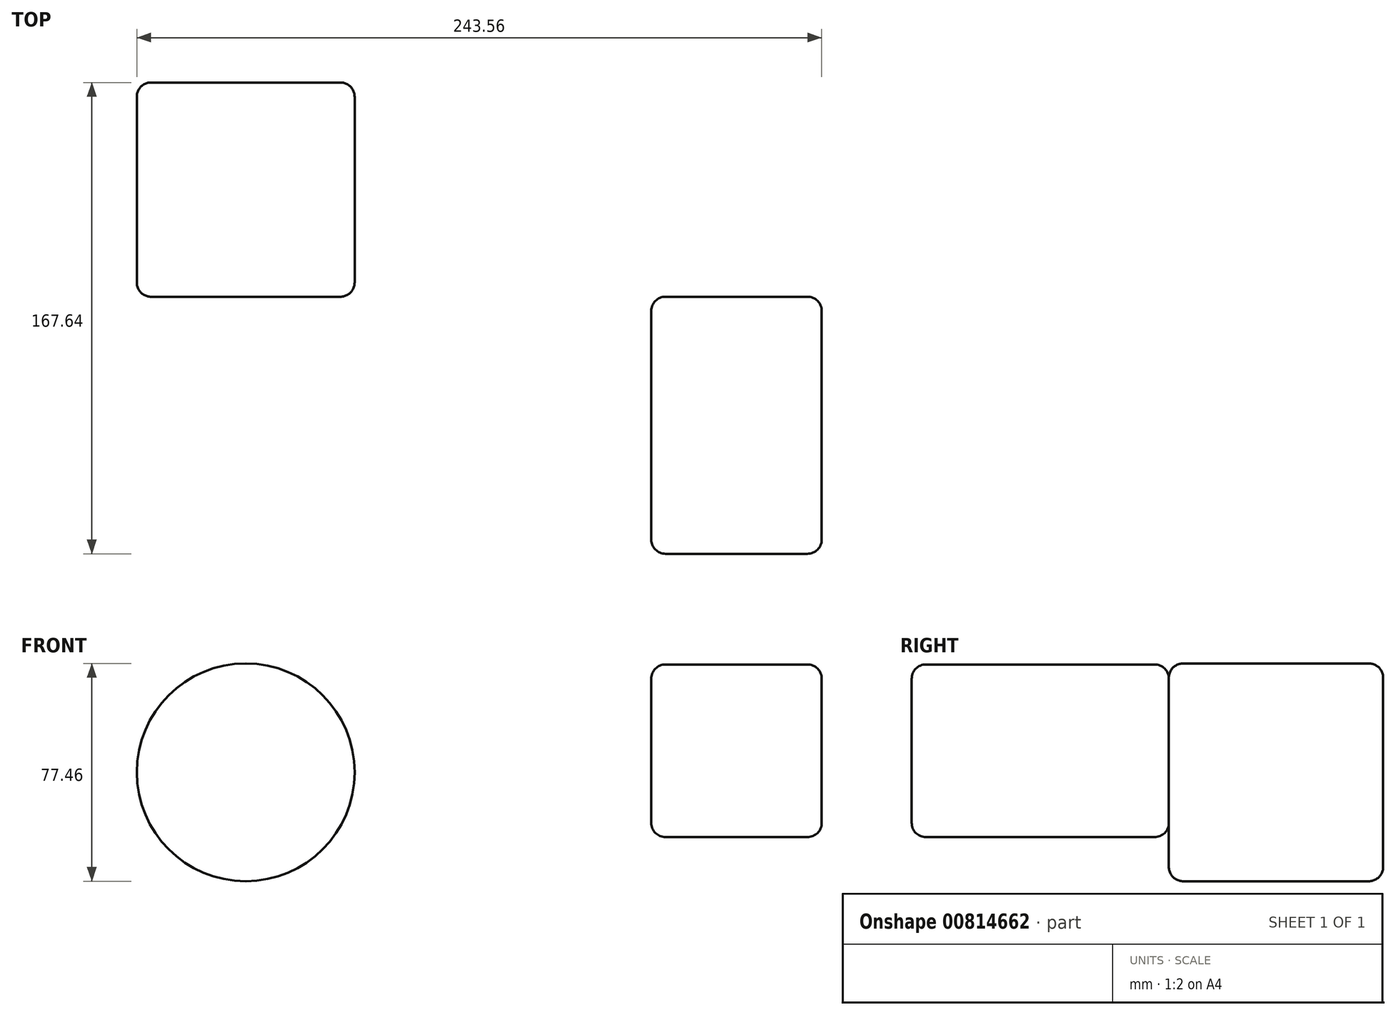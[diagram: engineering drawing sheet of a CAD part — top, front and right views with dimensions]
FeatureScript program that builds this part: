
annotation { "Feature Type Name" : "Feature", "Feature Type Description" : "" }
export const myFeature = defineFeature(function(context is Context, id is Id, definition is map)
    precondition{}
    {
        {
            var Q0;
            Q0=qCreatedBy(makeId("Front.planeOp"),FACE);
            var sketch = newSketch(context, id + "F0", { "sketchPlane" : qUnion([Q0])});
            skCircle(sketch, "E0", {"center": v(-110.61, 4.94) * mm, "radius": 38.73 * mm});
            skSolve(sketch);
        }
        {
            var Q0;
            Q0=makeQuery(id+"F0.imprint","IMPRINT",FACE,{"disambiguationData":[TD([[makeQuery(id+"F0.imprint","IMPRINT",EDGE,{"derivedFrom":sQuery(id+"F0.wireOp",EDGE,"E0")}),1.0]])]});
            extrude(context, id + "F1", {"entities" : qUnion([Q0]), "oppositeDirection" : true, "depth" : 76.2 * mm, "offsetDistance" : 25.4 * mm});
        }
        {
            var Q0;
            Q0=makeQuery(id+"F1.opExtrude","CAP_EDGE",EDGE,{"disambiguationData":[OSD([sQuery(id+"F0.wireOp",EDGE,"E0")])],"isStart":false});
            var Q1;
            Q1=makeQuery(id+"F1.opExtrude","CAP_EDGE",EDGE,{"disambiguationData":[OSD([sQuery(id+"F0.wireOp",EDGE,"E0")])],"isStart":true});
            fillet(context, id + "F2", {"entities" : qUnion([Q0, Q1]), "radius" : 5.08 * mm, "tangentPropagation" : true, "allowEdgeOverflow" : false});
        }
        {
            var Q0;
            Q0=qCreatedBy(makeId("Front.planeOp"),FACE);
            var sketch = newSketch(context, id + "F3", { "sketchPlane" : qUnion([Q0])});
            skLineSegment(sketch, "E1.bottom", {"start": v(94.22, 43.29) * mm, "end": v(33.6, 43.29) * mm});
            skLineSegment(sketch, "E1.top", {"start": v(94.22, -18.13) * mm, "end": v(33.6, -18.13) * mm});
            skLineSegment(sketch, "E1.left", {"start": v(94.22, 43.29) * mm, "end": v(94.22, -18.13) * mm});
            skLineSegment(sketch, "E1.right", {"start": v(33.6, 43.29) * mm, "end": v(33.6, -18.13) * mm});
            skSolve(sketch);
        }
        {
            var Q0;
            Q0=makeQuery(id+"F3.imprint","IMPRINT",FACE,{"disambiguationData":[TD([[makeQuery(id+"F3.imprint","IMPRINT",EDGE,{"derivedFrom":sQuery(id+"F3.wireOp",EDGE,"E1.bottom")}),1.0]])]});
            extrude(context, id + "F4", {"entities" : qUnion([Q0]), "depth" : 91.44 * mm, "offsetDistance" : 25.4 * mm});
        }
        {
            var Q0;
            Q0=makeQuery(id+"F4.opExtrude","CAP_EDGE",EDGE,{"disambiguationData":[OSD([sQuery(id+"F3.wireOp",EDGE,"E1.left")])],"isStart":false});
            var Q1;
            Q1=makeQuery(id+"F4.opExtrude","SWEPT_EDGE",EDGE,{"disambiguationData":[OSD([sQuery(id+"F3.wireOp",EDGE,"E1.top"),sQuery(id+"F3.wireOp",EDGE,"E1.left")])]});
            var Q2;
            Q2=makeQuery(id+"F4.opExtrude","CAP_EDGE",EDGE,{"disambiguationData":[OSD([sQuery(id+"F3.wireOp",EDGE,"E1.left")])],"isStart":true});
            var Q3;
            Q3=makeQuery(id+"F4.opExtrude","SWEPT_EDGE",EDGE,{"disambiguationData":[OSD([sQuery(id+"F3.wireOp",EDGE,"E1.bottom"),sQuery(id+"F3.wireOp",EDGE,"E1.left")])]});
            var Q4;
            Q4=makeQuery(id+"F4.opExtrude","CAP_EDGE",EDGE,{"disambiguationData":[OSD([sQuery(id+"F3.wireOp",EDGE,"E1.bottom")])],"isStart":true});
            var Q5;
            Q5=makeQuery(id+"F4.opExtrude","CAP_EDGE",EDGE,{"disambiguationData":[OSD([sQuery(id+"F3.wireOp",EDGE,"E1.right")])],"isStart":true});
            var Q6;
            Q6=makeQuery(id+"F4.opExtrude","CAP_EDGE",EDGE,{"disambiguationData":[OSD([sQuery(id+"F3.wireOp",EDGE,"E1.top")])],"isStart":true});
            var Q7;
            Q7=makeQuery(id+"F4.opExtrude","CAP_EDGE",EDGE,{"disambiguationData":[OSD([sQuery(id+"F3.wireOp",EDGE,"E1.right")])],"isStart":false});
            var Q8;
            Q8=makeQuery(id+"F4.opExtrude","SWEPT_EDGE",EDGE,{"disambiguationData":[OSD([sQuery(id+"F3.wireOp",EDGE,"E1.bottom"),sQuery(id+"F3.wireOp",EDGE,"E1.right")])]});
            var Q9;
            Q9=makeQuery(id+"F4.opExtrude","SWEPT_EDGE",EDGE,{"disambiguationData":[OSD([sQuery(id+"F3.wireOp",EDGE,"E1.top"),sQuery(id+"F3.wireOp",EDGE,"E1.right")])]});
            var Q10;
            Q10=makeQuery(id+"F4.opExtrude","CAP_EDGE",EDGE,{"disambiguationData":[OSD([sQuery(id+"F3.wireOp",EDGE,"E1.top")])],"isStart":false});
            var Q11;
            Q11=makeQuery(id+"F4.opExtrude","CAP_EDGE",EDGE,{"disambiguationData":[OSD([sQuery(id+"F3.wireOp",EDGE,"E1.bottom")])],"isStart":false});
            fillet(context, id + "F5", {"entities" : qUnion([Q0, Q1, Q2, Q3, Q4, Q5, Q6, Q7, Q8, Q9, Q10, Q11]), "radius" : 5.08 * mm, "tangentPropagation" : true, "allowEdgeOverflow" : false});
        }
    });
